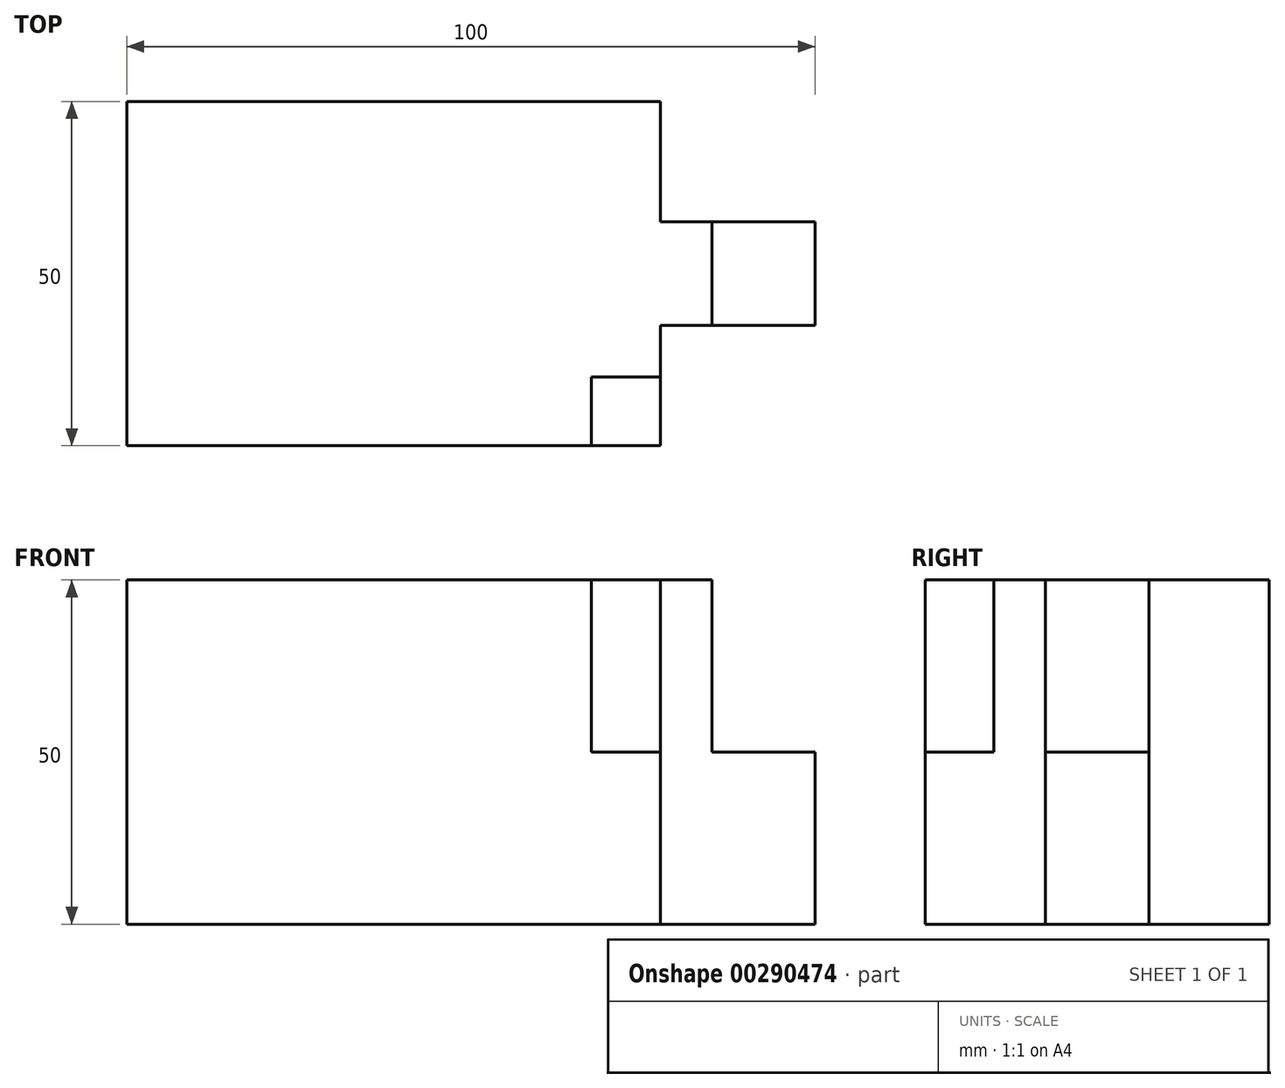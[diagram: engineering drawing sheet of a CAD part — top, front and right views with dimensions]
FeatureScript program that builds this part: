
annotation { "Feature Type Name" : "Feature", "Feature Type Description" : "" }
export const myFeature = defineFeature(function(context is Context, id is Id, definition is map)
    precondition{}
    {
        {
            var Q0;
            Q0=qCreatedBy(makeId("Front.planeOp"),FACE);
            var sketch = newSketch(context, id + "F0", { "sketchPlane" : qUnion([Q0])});
            skLineSegment(sketch, "E0", {"start": v(-50, 50) * mm, "end": v(-50, 0) * mm});
            skLineSegment(sketch, "E1", {"start": v(-50, 0) * mm, "end": v(50, 0) * mm});
            skLineSegment(sketch, "E2", {"start": v(50, 0) * mm, "end": v(50, 25) * mm});
            skLineSegment(sketch, "E3", {"start": v(50, 25) * mm, "end": v(35, 25) * mm});
            skLineSegment(sketch, "E4", {"start": v(35, 25) * mm, "end": v(35, 50) * mm});
            skLineSegment(sketch, "E5", {"start": v(35, 50) * mm, "end": v(-50, 50) * mm});
            skSolve(sketch);
        }
        {
            var Q0;
            Q0 = qSketchRegion(id + "F0", true);
            extrude(context, id + "F1", {"entities" : qUnion([Q0]), "endBound" : BoundingType.SYMMETRIC, "depth" : 50 * mm});
        }
        {
            var Q0;
            Q0=makeQuery(id+"F1.opExtrude","SWEPT_FACE",FACE,{"disambiguationData":[OSD([sQuery(id+"F0.wireOp",EDGE,"E5")])]});
            var sketch = newSketch(context, id + "F2", { "sketchPlane" : qUnion([Q0])});
            skLineSegment(sketch, "E6.bottom", {"start": v(27.5, 25) * mm, "end": v(50, 25) * mm});
            skLineSegment(sketch, "E6.top", {"start": v(27.5, 7.5) * mm, "end": v(50, 7.5) * mm});
            skLineSegment(sketch, "E6.left", {"start": v(27.5, 25) * mm, "end": v(27.5, 7.5) * mm});
            skLineSegment(sketch, "E6.right", {"start": v(50, 25) * mm, "end": v(50, 7.5) * mm});
            skLineSegment(sketch, "E7.bottom", {"start": v(27.5, -25) * mm, "end": v(50, -25) * mm});
            skLineSegment(sketch, "E7.top", {"start": v(27.5, -7.5) * mm, "end": v(50, -7.5) * mm});
            skLineSegment(sketch, "E7.left", {"start": v(27.5, -25) * mm, "end": v(27.5, -7.5) * mm});
            skLineSegment(sketch, "E7.right", {"start": v(50, -25) * mm, "end": v(50, -7.5) * mm});
            skSolve(sketch);
        }
        {
            var Q0;
            Q0 = qSketchRegion(id + "F2", true);
            var Q1;
            Q1=makeQuery(id+"F1.opExtrude","SWEPT_FACE",FACE,{"disambiguationData":[OSD([sQuery(id+"F0.wireOp",EDGE,"E1")])]});
            extrude(context, id + "F3", {"entities" : qUnion([Q0]), "operationType" : NewBodyOperationType.REMOVE, "endBound" : BoundingType.UP_TO_SURFACE, "oppositeDirection" : true, "endBoundEntityFace" : qUnion([Q1]), "depth" : 25 * mm});
        }
        {
            var Q0;
            Q0=makeQuery(id+"F1.opExtrude","SWEPT_FACE",FACE,{"disambiguationData":[OSD([sQuery(id+"F0.wireOp",EDGE,"E5")])]});
            var sketch = newSketch(context, id + "F4", { "sketchPlane" : qUnion([Q0])});
            skLineSegment(sketch, "E8.bottom", {"start": v(27.5, -25) * mm, "end": v(17.5, -25) * mm});
            skLineSegment(sketch, "E8.top", {"start": v(27.5, -15) * mm, "end": v(17.5, -15) * mm});
            skLineSegment(sketch, "E8.left", {"start": v(27.5, -25) * mm, "end": v(27.5, -15) * mm});
            skLineSegment(sketch, "E8.right", {"start": v(17.5, -25) * mm, "end": v(17.5, -15) * mm});
            skSolve(sketch);
        }
        {
            var Q0;
            Q0 = qSketchRegion(id + "F4", true);
            extrude(context, id + "F5", {"entities" : qUnion([Q0]), "operationType" : NewBodyOperationType.REMOVE, "oppositeDirection" : true, "depth" : 25 * mm});
        }
    });
